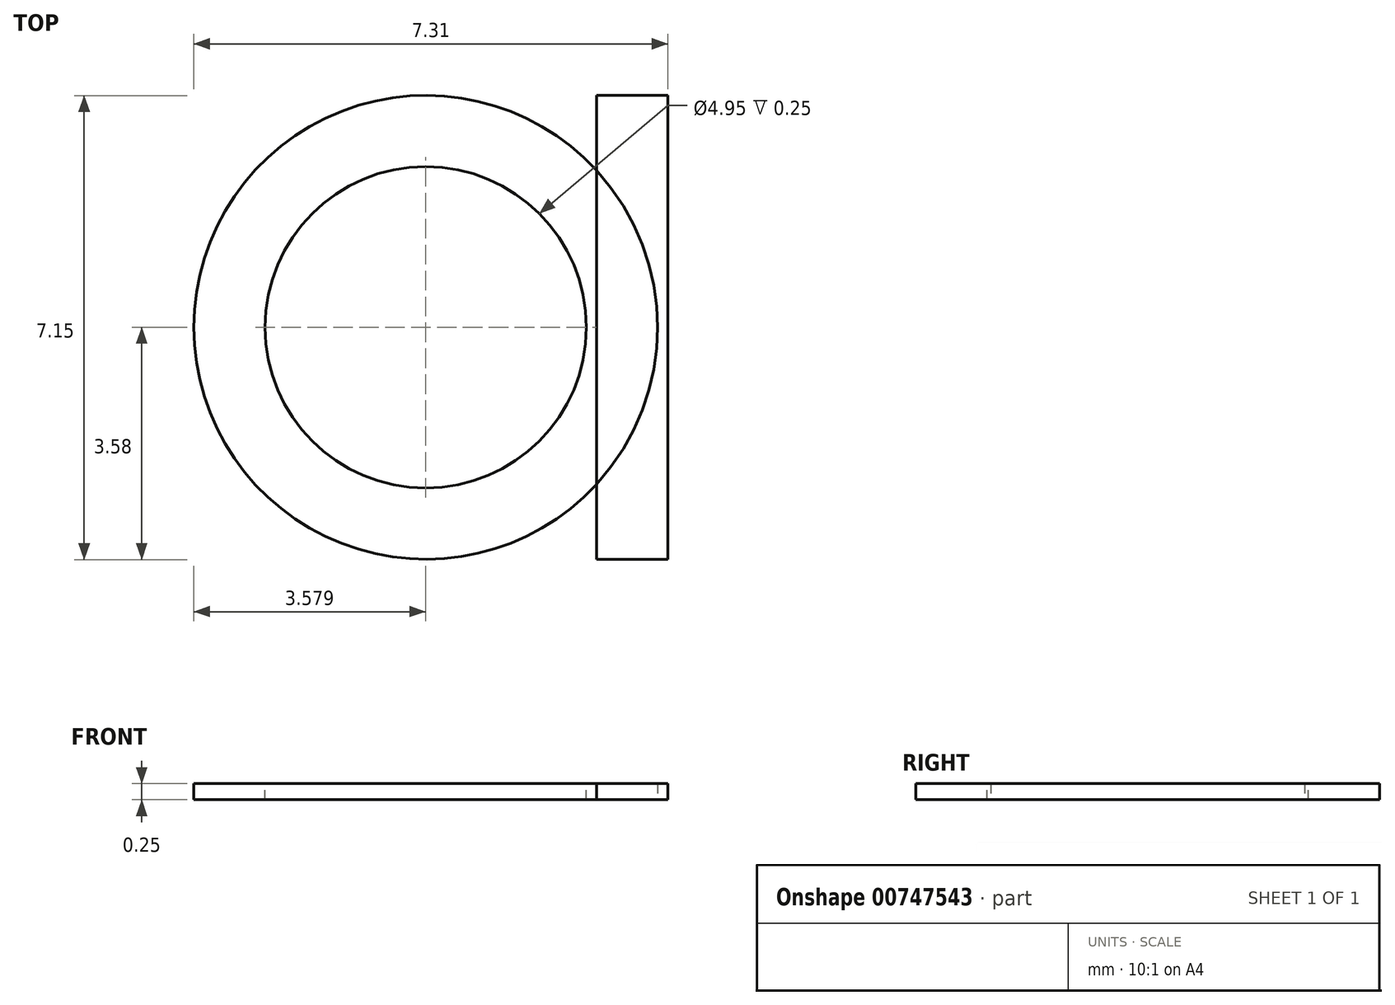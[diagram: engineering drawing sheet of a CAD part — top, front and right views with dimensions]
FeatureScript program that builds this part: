
annotation { "Feature Type Name" : "Feature", "Feature Type Description" : "" }
export const myFeature = defineFeature(function(context is Context, id is Id, definition is map)
    precondition{}
    {
        {
            var Q0;
            Q0=qCreatedBy(makeId("Top.planeOp"),FACE);
            var sketch = newSketch(context, id + "F0", { "sketchPlane" : qUnion([Q0])});
            skCircle(sketch, "E0", {"center": v(5.98, 0.02) * mm, "radius": 2.47 * mm});
            skCircle(sketch, "E1", {"center": v(5.98, 0.02) * mm, "radius": 3.57 * mm});
            skLineSegment(sketch, "E2.top", {"start": v(8.6, 3.6) * mm, "end": v(9.7, 3.6) * mm});
            skLineSegment(sketch, "E2.left", {"start": v(8.6, -3.56) * mm, "end": v(8.6, 3.6) * mm});
            skLineSegment(sketch, "E2.right", {"start": v(9.7, -3.56) * mm, "end": v(9.7, 3.6) * mm});
            skLineSegment(sketch, "E3", {"start": v(8.6, -3.56) * mm, "end": v(9.7, -3.56) * mm});
            skSolve(sketch);
        }
        {
            var Q0;
            Q0=makeQuery(id+"F0.imprint","IMPRINT",FACE,{"disambiguationData":[TD([[makeQuery(id+"F0.imprint","IMPRINT",EDGE,{"derivedFrom":sQuery(id+"F0.wireOp",EDGE,"E0")}),-1.0]])]});
            var Q1;
            Q1=makeQuery(id+"F0.imprint","IMPRINT",FACE,{"disambiguationData":[TD([[makeQuery(id+"F0.imprint","IMPRINT",EDGE,{"derivedFrom":sQuery(id+"F0.wireOp",EDGE,"E0")}),1.0]])]});
            var Q2;
            {var subQ0=sQuery(id+"F0.wireOp",EDGE,"E2.left");var subQ1=sQuery(id+"F0.wireOp",EDGE,"E1");var subQ2=makeQuery(id+"F0.imprint","INTERSECT",VERTEX,{"disambiguationData":[OD(0.0)],"derivedFrom":[subQ1,subQ0]});Q2=makeQuery(id+"F0.imprint","IMPRINT",FACE,{"disambiguationData":[TD([[makeQuery(id+"F0.imprint","IMPRINT",EDGE,{"disambiguationData":[TD([[subQ2,-1.0]])],"derivedFrom":subQ1}),1.0]])]});}
            extrude(context, id + "F1", {"entities" : qUnion([Q0, Q1, Q2]), "depth" : 0.25 * mm, "offsetDistance" : 25 * mm});
        }
        {
            var Q0;
            {var subQ1=sQuery(id+"F0.wireOp",EDGE,"E2.top");Q0=makeQuery(id+"F0.imprint","IMPRINT",FACE,{"disambiguationData":[TD([[makeQuery(id+"F0.imprint","IMPRINT",EDGE,{"derivedFrom":subQ1}),-1.0]])]});}
            extrude(context, id + "F2", {"entities" : qUnion([Q0]), "operationType" : NewBodyOperationType.ADD, "depth" : 0.25 * mm, "offsetDistance" : 25 * mm});
        }
        {
            var Q0;
            {var subQ0=sQuery(id+"F0.wireOp",EDGE,"E1");Q0=makeQuery(id+"F2.boolean.opBoolean","MERGE",FACE,{"derivedFrom":[makeQuery(id+"F1.opExtrude","CAP_FACE",FACE,{"disambiguationData":[OSD([subQ0])],"isStart":false}),makeQuery(id+"F2.opExtrude","CAP_FACE",FACE,{"disambiguationData":[OSD([subQ0,sQuery(id+"F0.wireOp",EDGE,"E2.top"),sQuery(id+"F0.wireOp",EDGE,"E2.left"),sQuery(id+"F0.wireOp",EDGE,"E2.right"),sQuery(id+"F0.wireOp",EDGE,"E3")])],"isStart":false})]});}
            var sketch = newSketch(context, id + "F3", { "sketchPlane" : qUnion([Q0])});
            skCircle(sketch, "E4", {"center": v(5.98, 0.02) * mm, "radius": 2.48 * mm});
            skSolve(sketch);
        }
        {
            var Q0;
            Q0=makeQuery(id+"F3.imprint","IMPRINT",FACE,{"disambiguationData":[TD([[makeQuery(id+"F3.imprint","IMPRINT",EDGE,{"derivedFrom":sQuery(id+"F3.wireOp",EDGE,"E4")}),1.0]])]});
            extrude(context, id + "F4", {"entities" : qUnion([Q0]), "operationType" : NewBodyOperationType.REMOVE, "oppositeDirection" : true, "depth" : 0.25 * mm, "offsetDistance" : 25 * mm});
        }
    });
